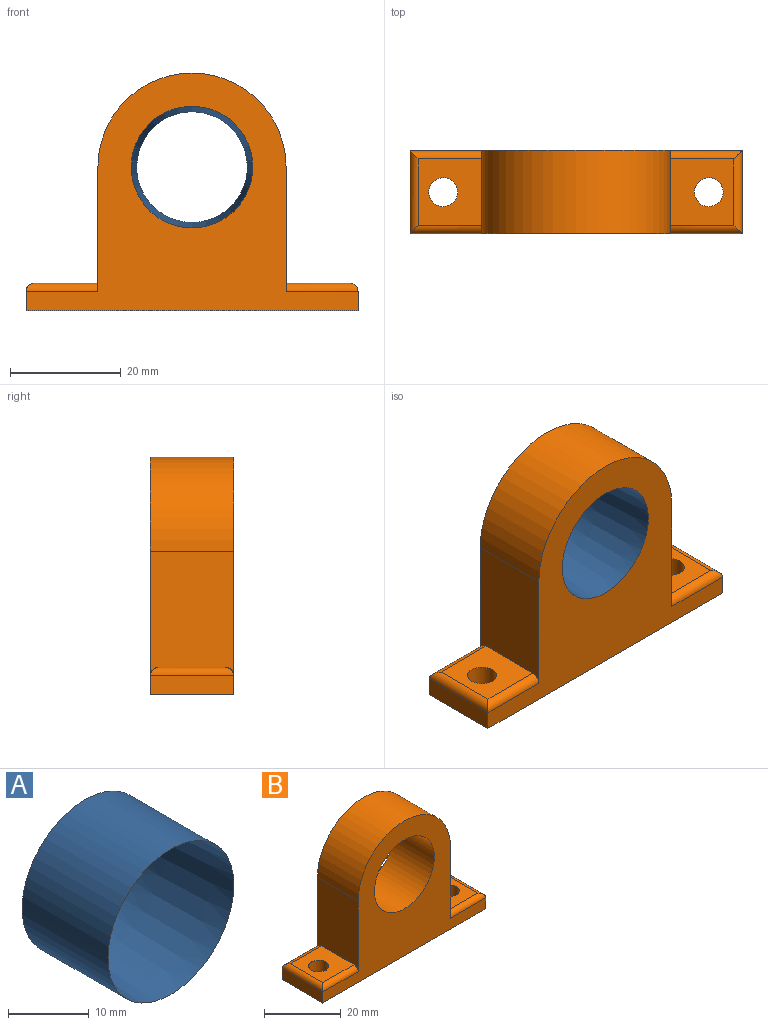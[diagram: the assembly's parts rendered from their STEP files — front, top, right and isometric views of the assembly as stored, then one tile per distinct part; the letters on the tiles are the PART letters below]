
ASSEMBLY  parts=2 mates=1
PART A: 3 faces, bbox 22x15x22 mm
  f0: cylinder r=11mm len=22mm, axis (0,-1,0), area 1036.7mm2, adj f1,f2
  f1: cone r=11mm half-angle=3.8deg, axis (0,-1,0), area 991.8mm2, adj f0,f2
  f2: plane 22x22mm, normal (0,1,0), area 66mm2, adj f0,f1
PART B: 19 faces, bbox 60x15x43 mm
  f0: plane 60x15mm, normal (0,0,-1), area 857.5mm2, adj f1,f8,f9,f10,f11,f12
  f1: plane 15x3.5mm, normal (1,0,0), area 52.5mm2, adj f0,f9,f10,f15
  f2: plane 12x11.5mm, normal (0,0,1), area 116.8mm2, adj f3,f12,f13,f14,f15
  f3: plane 22.5x15mm, normal (1,0,0), area 316mm2, adj f2,f4,f9,f10,f13,f14
  f4: cylinder r=17mm len=34mm, axis (0,-1,0), area 801.1mm2, adj f3,f5,f9,f10
  f5: plane 22.5x15mm, normal (-1,0,0), area 316mm2, adj f4,f6,f9,f10,f16,f17
  f6: plane 12x11.5mm, normal (0,0,1), area 116.8mm2, adj f5,f11,f16,f17,f18
  f7: cylinder r=11mm len=22mm, axis (0,-1,0), area 1036.7mm2, adj f9,f10
  f8: plane 15x3.5mm, normal (-1,0,0), area 52.5mm2, adj f0,f9,f10,f18
  f9: plane 60x43mm, normal (0,1,0), area 1048.8mm2, adj f0,f1,f3,f4,f5,f7,f8,f13
  f10: plane 60x43mm, normal (0,-1,0), area 1048.8mm2, adj f0,f1,f3,f4,f5,f7,f8,f14
  f11: cylinder r=2.6mm len=5.2mm, axis (0,0,-1), area 81.7mm2, adj f0,f6
  f12: cylinder r=2.6mm len=5.2mm, axis (0,0,-1), area 81.7mm2, adj f0,f2
  f13: cylinder r=1.5mm len=13mm, axis (1,0,0), area 29.3mm2, adj f2,f3,f9,f15
  f14: cylinder r=1.5mm len=13mm, axis (-1,0,0), area 29.3mm2, adj f2,f3,f10,f15
  f15: cylinder r=1.5mm len=15mm, axis (0,1,0), area 32.8mm2, adj f1,f2,f13,f14
  f16: cylinder r=1.5mm len=13mm, axis (1,0,0), area 29.3mm2, adj f5,f6,f9,f18
  f17: cylinder r=1.5mm len=13mm, axis (-1,0,0), area 29.3mm2, adj f5,f6,f10,f18
  f18: cylinder r=1.5mm len=15mm, axis (0,-1,0), area 32.8mm2, adj f6,f8,f16,f17
PLACE A t=(22.06,-7.5,28.63)mm
PLACE B t=(-7.94,-7.5,2.63)mm
MATE cylindrical A.f0 <-> B.f4  axis (0,1,0) through (22.06,7.5,28.63)mm
